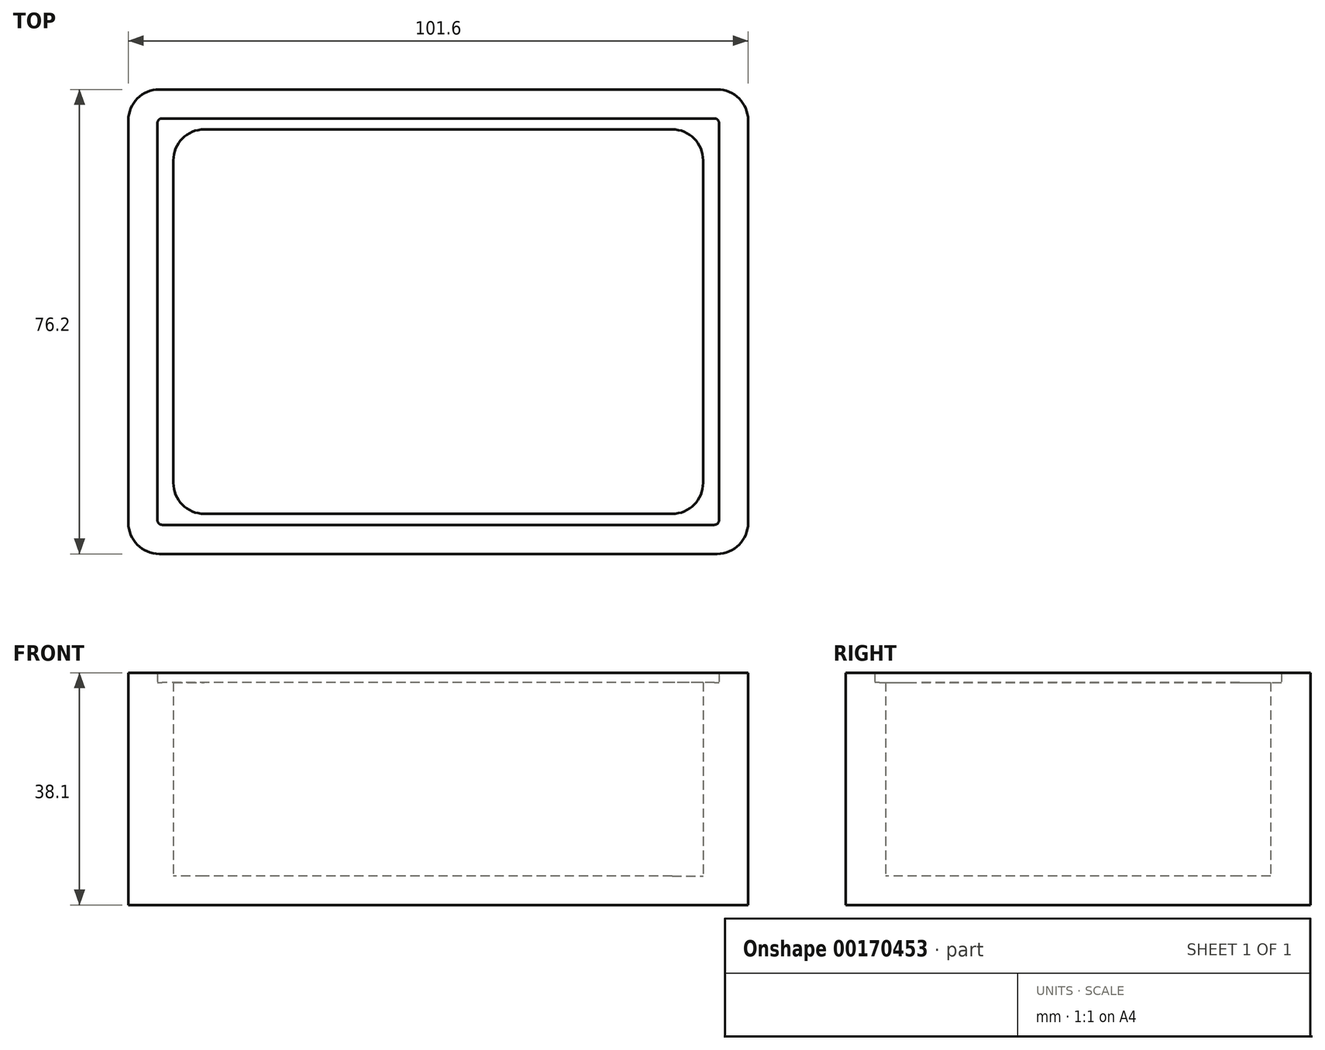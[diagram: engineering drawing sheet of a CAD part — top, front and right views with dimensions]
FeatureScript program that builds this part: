
annotation { "Feature Type Name" : "Feature", "Feature Type Description" : "" }
export const myFeature = defineFeature(function(context is Context, id is Id, definition is map)
    precondition{}
    {
        {
            var Q0;
            Q0=qCreatedBy(makeId("Top.planeOp"),FACE);
            var sketch = newSketch(context, id + "F0", { "sketchPlane" : qUnion([Q0])});
            skLineSegment(sketch, "E0.bottom", {"start": v(50.8, -38.1) * mm, "end": v(-50.8, -38.1) * mm});
            skLineSegment(sketch, "E0.top", {"start": v(50.8, 38.1) * mm, "end": v(-50.8, 38.1) * mm});
            skLineSegment(sketch, "E0.left", {"start": v(50.8, -38.1) * mm, "end": v(50.8, 38.1) * mm});
            skLineSegment(sketch, "E0.right", {"start": v(-50.8, -38.1) * mm, "end": v(-50.8, 38.1) * mm});
            skPoint(sketch, "E0.middle", {"position": v(0, 0) * mm});
            skSolve(sketch);
        }
        {
            var Q0;
            Q0=makeQuery(id+"F0.imprint","IMPRINT",FACE,{"disambiguationData":[TD([[makeQuery(id+"F0.imprint","IMPRINT",EDGE,{"derivedFrom":sQuery(id+"F0.wireOp",EDGE,"E0.bottom")}),-1.0]])]});
            extrude(context, id + "F1", {"entities" : qUnion([Q0]), "depth" : 38.1 * mm});
        }
        {
            var Q0;
            Q0=makeQuery(id+"F1.opExtrude","CAP_FACE",FACE,{"disambiguationData":[OSD([sQuery(id+"F0.wireOp",EDGE,"E0.bottom"),sQuery(id+"F0.wireOp",EDGE,"E0.top"),sQuery(id+"F0.wireOp",EDGE,"E0.left"),sQuery(id+"F0.wireOp",EDGE,"E0.right")])],"isStart":false});
            shell(context, id + "F2", {"entities" : qUnion([Q0]), "thickness" : 4.76 * mm});
        }
        {
            var Q0;
            Q0=makeQuery(id+"F2.opShell","OFFSET_FACE",FACE,{"disambiguationData":[OSD([sQuery(id+"F0.wireOp",EDGE,"E0.bottom"),sQuery(id+"F0.wireOp",EDGE,"E0.top"),sQuery(id+"F0.wireOp",EDGE,"E0.left"),sQuery(id+"F0.wireOp",EDGE,"E0.right")])]});
            var sketch = newSketch(context, id + "F3", { "sketchPlane" : qUnion([Q0])});
            skLineSegment(sketch, "E1.0.0", {"start": v(46.04, -33.34) * mm, "end": v(46.04, 33.34) * mm});
            skLineSegment(sketch, "E1.0.1", {"start": v(46.04, 33.34) * mm, "end": v(-46.04, 33.34) * mm});
            skLineSegment(sketch, "E1.0.2", {"start": v(-46.04, 33.34) * mm, "end": v(-46.04, -33.34) * mm});
            skLineSegment(sketch, "E1.0.3", {"start": v(-46.04, -33.34) * mm, "end": v(46.04, -33.34) * mm});
            skLineSegment(sketch, "E2.bottom", {"start": v(43.42, 31.53) * mm, "end": v(-43.42, 31.53) * mm});
            skLineSegment(sketch, "E2.top", {"start": v(43.42, -31.53) * mm, "end": v(-43.42, -31.53) * mm});
            skLineSegment(sketch, "E2.left", {"start": v(43.42, 31.53) * mm, "end": v(43.42, -31.53) * mm});
            skLineSegment(sketch, "E2.right", {"start": v(-43.42, 31.53) * mm, "end": v(-43.42, -31.53) * mm});
            skPoint(sketch, "E2.middle", {"position": v(0, 0) * mm});
            skSolve(sketch);
        }
        {
            var Q0;
            Q0 = qSketchRegion(id + "F3", true);
            extrude(context, id + "F4", {"entities" : qUnion([Q0]), "operationType" : NewBodyOperationType.ADD, "depth" : 31.75 * mm});
        }
        {
            var Q0;
            Q0=makeQuery(id+"F2.opShell","OFFSET_EDGE",EDGE,{"disambiguationData":[OSD([sQuery(id+"F0.wireOp",EDGE,"E0.top"),sQuery(id+"F0.wireOp",EDGE,"E0.right")])]});
            var Q1;
            Q1=makeQuery(id+"F2.opShell","OFFSET_EDGE",EDGE,{"disambiguationData":[OSD([sQuery(id+"F0.wireOp",EDGE,"E0.top"),sQuery(id+"F0.wireOp",EDGE,"E0.left")])]});
            var Q2;
            Q2=makeQuery(id+"F2.opShell","OFFSET_EDGE",EDGE,{"disambiguationData":[OSD([sQuery(id+"F0.wireOp",EDGE,"E0.bottom"),sQuery(id+"F0.wireOp",EDGE,"E0.left")])]});
            var Q3;
            Q3=makeQuery(id+"F2.opShell","OFFSET_EDGE",EDGE,{"disambiguationData":[OSD([sQuery(id+"F0.wireOp",EDGE,"E0.bottom"),sQuery(id+"F0.wireOp",EDGE,"E0.right")])]});
            fillet(context, id + "F5", {"entities" : qUnion([Q0, Q1, Q2, Q3]), "radius" : 0.76 * mm, "tangentPropagation" : true, "allowEdgeOverflow" : false});
        }
        {
            var Q0;
            Q0=makeQuery(id+"F4.opExtrude","SWEPT_EDGE",EDGE,{"disambiguationData":[OSD([sQuery(id+"F3.wireOp",EDGE,"E2.bottom"),sQuery(id+"F3.wireOp",EDGE,"E2.left")])]});
            var Q1;
            Q1=makeQuery(id+"F4.opExtrude","SWEPT_EDGE",EDGE,{"disambiguationData":[OSD([sQuery(id+"F3.wireOp",EDGE,"E2.top"),sQuery(id+"F3.wireOp",EDGE,"E2.left")])]});
            var Q2;
            Q2=makeQuery(id+"F4.opExtrude","SWEPT_EDGE",EDGE,{"disambiguationData":[OSD([sQuery(id+"F3.wireOp",EDGE,"E2.top"),sQuery(id+"F3.wireOp",EDGE,"E2.right")])]});
            var Q3;
            Q3=makeQuery(id+"F4.opExtrude","SWEPT_EDGE",EDGE,{"disambiguationData":[OSD([sQuery(id+"F3.wireOp",EDGE,"E2.bottom"),sQuery(id+"F3.wireOp",EDGE,"E2.right")])]});
            fillet(context, id + "F6", {"entities" : qUnion([Q0, Q1, Q2, Q3]), "radius" : 5.08 * mm, "tangentPropagation" : true, "allowEdgeOverflow" : false});
        }
        {
            var Q0;
            Q0=makeQuery(id+"F1.opExtrude","SWEPT_EDGE",EDGE,{"disambiguationData":[OSD([sQuery(id+"F0.wireOp",EDGE,"E0.top"),sQuery(id+"F0.wireOp",EDGE,"E0.left")])]});
            var Q1;
            Q1=makeQuery(id+"F1.opExtrude","SWEPT_EDGE",EDGE,{"disambiguationData":[OSD([sQuery(id+"F0.wireOp",EDGE,"E0.bottom"),sQuery(id+"F0.wireOp",EDGE,"E0.left")])]});
            var Q2;
            Q2=makeQuery(id+"F1.opExtrude","SWEPT_EDGE",EDGE,{"disambiguationData":[OSD([sQuery(id+"F0.wireOp",EDGE,"E0.top"),sQuery(id+"F0.wireOp",EDGE,"E0.right")])]});
            var Q3;
            Q3=makeQuery(id+"F1.opExtrude","SWEPT_EDGE",EDGE,{"disambiguationData":[OSD([sQuery(id+"F0.wireOp",EDGE,"E0.bottom"),sQuery(id+"F0.wireOp",EDGE,"E0.right")])]});
            fillet(context, id + "F7", {"entities" : qUnion([Q0, Q1, Q2, Q3]), "radius" : 5.08 * mm, "tangentPropagation" : true, "allowEdgeOverflow" : false});
        }
    });
